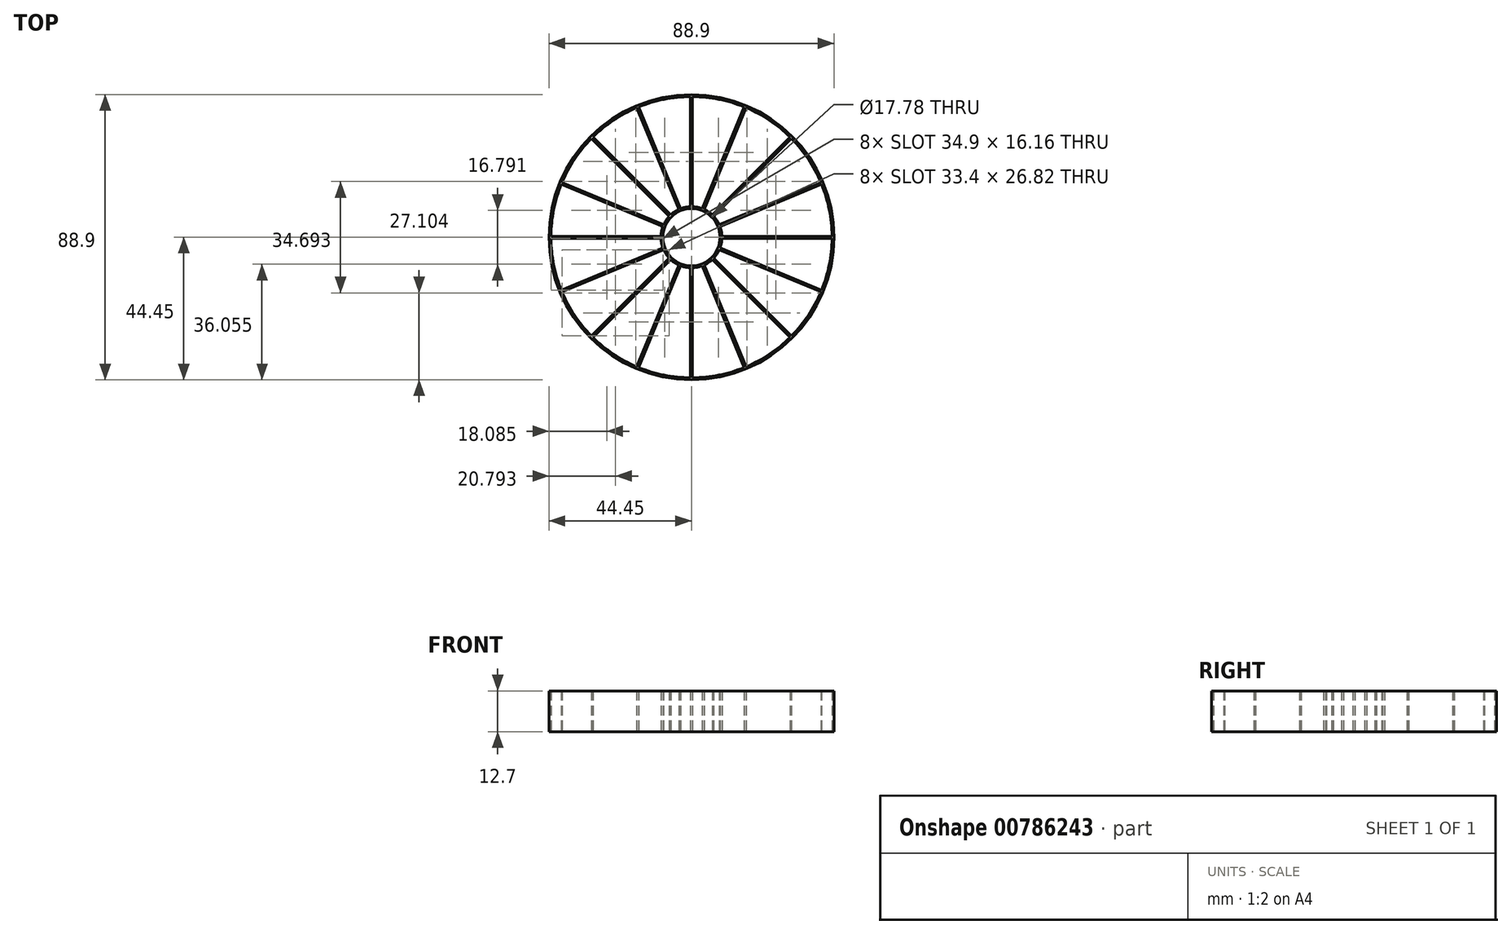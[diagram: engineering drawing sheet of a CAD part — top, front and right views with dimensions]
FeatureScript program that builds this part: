
annotation { "Feature Type Name" : "Feature", "Feature Type Description" : "" }
export const myFeature = defineFeature(function(context is Context, id is Id, definition is map)
    precondition{}
    {
        {
            var Q0;
            Q0=qCreatedBy(makeId("Top.planeOp"),FACE);
            var sketch = newSketch(context, id + "F0", { "sketchPlane" : qUnion([Q0])});
            skCircle(sketch, "E0", {"center": v(0, 0) * mm, "radius": 44.45 * mm});
            skArc(sketch, "E1", {"start": v(-0.32, 43.81) * mm, "mid": v(-8.55, 42.97) * mm, "end": v(-16.47, 40.6) * mm});
            skLineSegment(sketch, "E2", {"start": v(-44.45, 0) * mm, "end": v(44.45, 0) * mm, "construction": true});
            skLineSegment(sketch, "E3", {"start": v(-31.43, -31.43) * mm, "end": v(31.43, 31.43) * mm, "construction": true});
            skLineSegment(sketch, "E4", {"start": v(0, 44.45) * mm, "end": v(0, -44.45) * mm, "construction": true});
            skLineSegment(sketch, "E5", {"start": v(-30.98, 30.98) * mm, "end": v(30.98, -30.98) * mm, "construction": true});
            skArc(sketch, "E6", {"start": v(9.52, 0.32) * mm, "mid": v(6.74, 6.74) * mm, "end": v(0.32, 9.52) * mm});
            skCircle(sketch, "E7", {"center": v(0, 0) * mm, "radius": 8.9 * mm});
            skLineSegment(sketch, "E8", {"start": v(0.32, 9.52) * mm, "end": v(0.32, 43.81) * mm});
            skLineSegment(sketch, "E9", {"start": v(-0.32, 43.81) * mm, "end": v(-0.32, 9.52) * mm});
            skLineSegment(sketch, "E10", {"start": v(-43.81, 0.32) * mm, "end": v(-9.52, 0.32) * mm});
            skLineSegment(sketch, "E11", {"start": v(-43.81, -0.32) * mm, "end": v(-9.52, -0.32) * mm});
            skLineSegment(sketch, "E12", {"start": v(9.52, 0.32) * mm, "end": v(43.81, 0.32) * mm});
            skLineSegment(sketch, "E13", {"start": v(9.52, -0.32) * mm, "end": v(43.81, -0.32) * mm});
            skLineSegment(sketch, "E14", {"start": v(0.32, -9.52) * mm, "end": v(0.32, -43.81) * mm});
            skLineSegment(sketch, "E15", {"start": v(-0.32, -9.52) * mm, "end": v(-0.32, -43.81) * mm});
            skArc(sketch, "E16.trimOffspring", {"start": v(43.81, 0.32) * mm, "mid": v(42.97, 8.55) * mm, "end": v(40.6, 16.47) * mm});
            skArc(sketch, "E17.trimOffspring", {"start": v(0.32, -43.81) * mm, "mid": v(8.55, -42.97) * mm, "end": v(16.47, -40.6) * mm});
            skArc(sketch, "E18.trimOffspring", {"start": v(-43.81, -0.32) * mm, "mid": v(-42.97, -8.55) * mm, "end": v(-40.6, -16.47) * mm});
            skArc(sketch, "E19.trimOffspring", {"start": v(-0.32, 9.52) * mm, "mid": v(-6.74, 6.74) * mm, "end": v(-9.52, 0.32) * mm});
            skArc(sketch, "E20.trimOffspring", {"start": v(-9.52, -0.32) * mm, "mid": v(-6.74, -6.74) * mm, "end": v(-0.32, -9.52) * mm});
            skArc(sketch, "E21.trimOffspring", {"start": v(0.32, -9.52) * mm, "mid": v(6.74, -6.74) * mm, "end": v(9.52, -0.32) * mm});
            skLineSegment(sketch, "E22", {"start": v(-16.77, 40.48) * mm, "end": v(16.77, -40.48) * mm, "construction": true});
            skLineSegment(sketch, "E23.MirrorCS", {"start": v(-30.76, 31.2) * mm, "end": v(-6.5, 6.96) * mm});
            skLineSegment(sketch, "E24.MirrorCS", {"start": v(-6.96, 6.5) * mm, "end": v(-31.2, 30.76) * mm});
            skLineSegment(sketch, "E25.MirrorCS", {"start": v(6.96, -6.5) * mm, "end": v(31.2, -30.76) * mm});
            skLineSegment(sketch, "E26.MirrorCS", {"start": v(6.5, -6.96) * mm, "end": v(30.76, -31.2) * mm});
            skLineSegment(sketch, "E27.MirrorCS", {"start": v(-6.96, -6.5) * mm, "end": v(-31.2, -30.76) * mm});
            skLineSegment(sketch, "E28.MirrorCS", {"start": v(-6.5, -6.96) * mm, "end": v(-30.76, -31.2) * mm});
            skLineSegment(sketch, "E29.MirrorCS", {"start": v(31.2, 30.76) * mm, "end": v(6.96, 6.5) * mm});
            skLineSegment(sketch, "E30.MirrorCS", {"start": v(30.76, 31.2) * mm, "end": v(6.5, 6.96) * mm});
            skLineSegment(sketch, "E31", {"start": v(-8.55, 42.97) * mm, "end": v(8.55, -42.97) * mm, "construction": true});
            skLineSegment(sketch, "E32.MirrorCS", {"start": v(-16.47, 40.6) * mm, "end": v(-3.35, 8.92) * mm});
            skLineSegment(sketch, "E33.MirrorCS", {"start": v(-3.94, 8.67) * mm, "end": v(-17.06, 40.36) * mm});
            skLineSegment(sketch, "E34.MirrorCS", {"start": v(16.47, 40.6) * mm, "end": v(3.35, 8.92) * mm});
            skLineSegment(sketch, "E35.MirrorCS", {"start": v(3.94, 8.67) * mm, "end": v(17.06, 40.36) * mm});
            skLineSegment(sketch, "E36.MirrorCS", {"start": v(-40.36, 17.06) * mm, "end": v(-8.67, 3.94) * mm});
            skLineSegment(sketch, "E37.MirrorCS", {"start": v(-40.6, 16.47) * mm, "end": v(-8.92, 3.35) * mm});
            skLineSegment(sketch, "E38.MirrorCS", {"start": v(40.6, 16.47) * mm, "end": v(8.92, 3.35) * mm});
            skLineSegment(sketch, "E39.MirrorCS", {"start": v(40.36, 17.06) * mm, "end": v(8.67, 3.94) * mm});
            skLineSegment(sketch, "E40.MirrorCS", {"start": v(-8.67, -3.94) * mm, "end": v(-40.36, -17.06) * mm});
            skLineSegment(sketch, "E41.MirrorCS", {"start": v(-8.92, -3.35) * mm, "end": v(-40.6, -16.47) * mm});
            skLineSegment(sketch, "E42.MirrorCS", {"start": v(8.92, -3.35) * mm, "end": v(40.6, -16.47) * mm});
            skLineSegment(sketch, "E43.MirrorCS", {"start": v(8.67, -3.94) * mm, "end": v(40.36, -17.06) * mm});
            skLineSegment(sketch, "E44.MirrorCS", {"start": v(-3.94, -8.67) * mm, "end": v(-17.06, -40.36) * mm});
            skLineSegment(sketch, "E45.MirrorCS", {"start": v(-3.35, -8.92) * mm, "end": v(-16.47, -40.6) * mm});
            skLineSegment(sketch, "E46.MirrorCS", {"start": v(3.94, -8.67) * mm, "end": v(17.06, -40.36) * mm});
            skLineSegment(sketch, "E47.MirrorCS", {"start": v(3.35, -8.92) * mm, "end": v(16.47, -40.6) * mm});
            skArc(sketch, "E48.trimOffspring", {"start": v(-17.06, 40.36) * mm, "mid": v(-24.34, 36.43) * mm, "end": v(-30.76, 31.2) * mm});
            skArc(sketch, "E49.trimOffspring", {"start": v(16.47, 40.6) * mm, "mid": v(8.55, 42.97) * mm, "end": v(0.32, 43.81) * mm});
            skArc(sketch, "E50.trimOffspring", {"start": v(30.76, 31.2) * mm, "mid": v(24.34, 36.43) * mm, "end": v(17.06, 40.36) * mm});
            skArc(sketch, "E51.trimOffspring", {"start": v(40.36, 17.06) * mm, "mid": v(36.43, 24.34) * mm, "end": v(31.2, 30.76) * mm});
            skArc(sketch, "E52.trimOffspring", {"start": v(40.6, -16.47) * mm, "mid": v(42.97, -8.55) * mm, "end": v(43.81, -0.32) * mm});
            skArc(sketch, "E53.trimOffspring", {"start": v(31.2, -30.76) * mm, "mid": v(36.43, -24.34) * mm, "end": v(40.36, -17.06) * mm});
            skArc(sketch, "E54.trimOffspring", {"start": v(17.06, -40.36) * mm, "mid": v(24.34, -36.43) * mm, "end": v(30.76, -31.2) * mm});
            skArc(sketch, "E55.trimOffspring", {"start": v(-16.47, -40.6) * mm, "mid": v(-8.55, -42.97) * mm, "end": v(-0.32, -43.81) * mm});
            skArc(sketch, "E56.trimOffspring", {"start": v(-30.76, -31.2) * mm, "mid": v(-24.34, -36.43) * mm, "end": v(-17.06, -40.36) * mm});
            skArc(sketch, "E57.trimOffspring", {"start": v(-40.36, -17.06) * mm, "mid": v(-36.43, -24.34) * mm, "end": v(-31.2, -30.76) * mm});
            skArc(sketch, "E58.trimOffspring", {"start": v(-40.6, 16.47) * mm, "mid": v(-42.97, 8.55) * mm, "end": v(-43.81, 0.32) * mm});
            skArc(sketch, "E59.trimOffspring", {"start": v(-31.2, 30.76) * mm, "mid": v(-36.43, 24.34) * mm, "end": v(-40.36, 17.06) * mm});
            skSolve(sketch);
        }
        {
            var Q0;
            Q0=makeQuery(id+"F0.imprint","IMPRINT",FACE,{"disambiguationData":[TD([[makeQuery(id+"F0.imprint","IMPRINT",EDGE,{"derivedFrom":sQuery(id+"F0.wireOp",EDGE,"E0")}),1.0]])]});
            extrude(context, id + "F1", {"entities" : qUnion([Q0]), "depth" : 12.7 * mm, "offsetDistance" : 25.4 * mm});
        }
    });
